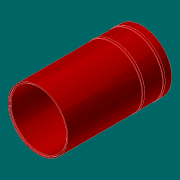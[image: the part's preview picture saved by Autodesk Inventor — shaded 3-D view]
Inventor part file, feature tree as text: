
AUTODESK INVENTOR PART (.ipt)
format: ipt  version: 2017.3 (Build 213257000, 257)  size: 166,400 bytes
history: native  units: in
note: dims shown in document units (in); Inventor stores cm internally (conversion verified against a paired STEP export)
features: extrude x5, sketch x5, fillet x3, plane x1, chamfer x1
ambient origin geometry x8: Origin, YZ Plane, XZ Plane, XY Plane, X Axis, Y Axis, Z Axis, Center Point
bodies: Solid1 (feature_tree)
feature tree (15):
  extrude  "Extrusion1"  Depth=30.5in
  extrude  "Extrusion2"  Depth=53.2283in
  fillet  "Fillet1"  Radius=4.5in
  plane  "Work Plane1"
  extrude  "Extrusion3"  [1 undecoded]
  extrude  "Extrusion4"  Depth=1.0in TaperAngle=0.0deg
  extrude  "Extrusion5"  Depth=0.0312in
  fillet  "Fillet2"  Radius=3.5in
  fillet  "Fillet3"  Radius=0.0312in
  chamfer  "Chamfer2"  Distance=29.5in
  sketch  "Sketch1"  dims[d0=28.5in d1=30.5in]
  sketch  "Sketch2"  dims[d2=53.2283in d3=0.0in d4=30.75in d5=4.5in d6=0.0in]
  sketch  "Sketch3"  dims[d7=0.1875in d11=-15.0394in]
  sketch  "Sketch4"  dims[d12=30.855in d13=1.0in d14=0.0in]
  sketch  "Sketch5"  dims[d15=0.1875in d16=30.516in d17=3.5in d18=0.0in d19=0.0312in d20=29.5in d21=0.5in d22=0.0in d23=0.0312in d24=0.125in d25=45.0deg]
note: 1 required parameter value undecoded (feature->parameter linkage not recoverable at this tier; creation-order binding heuristic only, values carry confidence <= 0.55)
